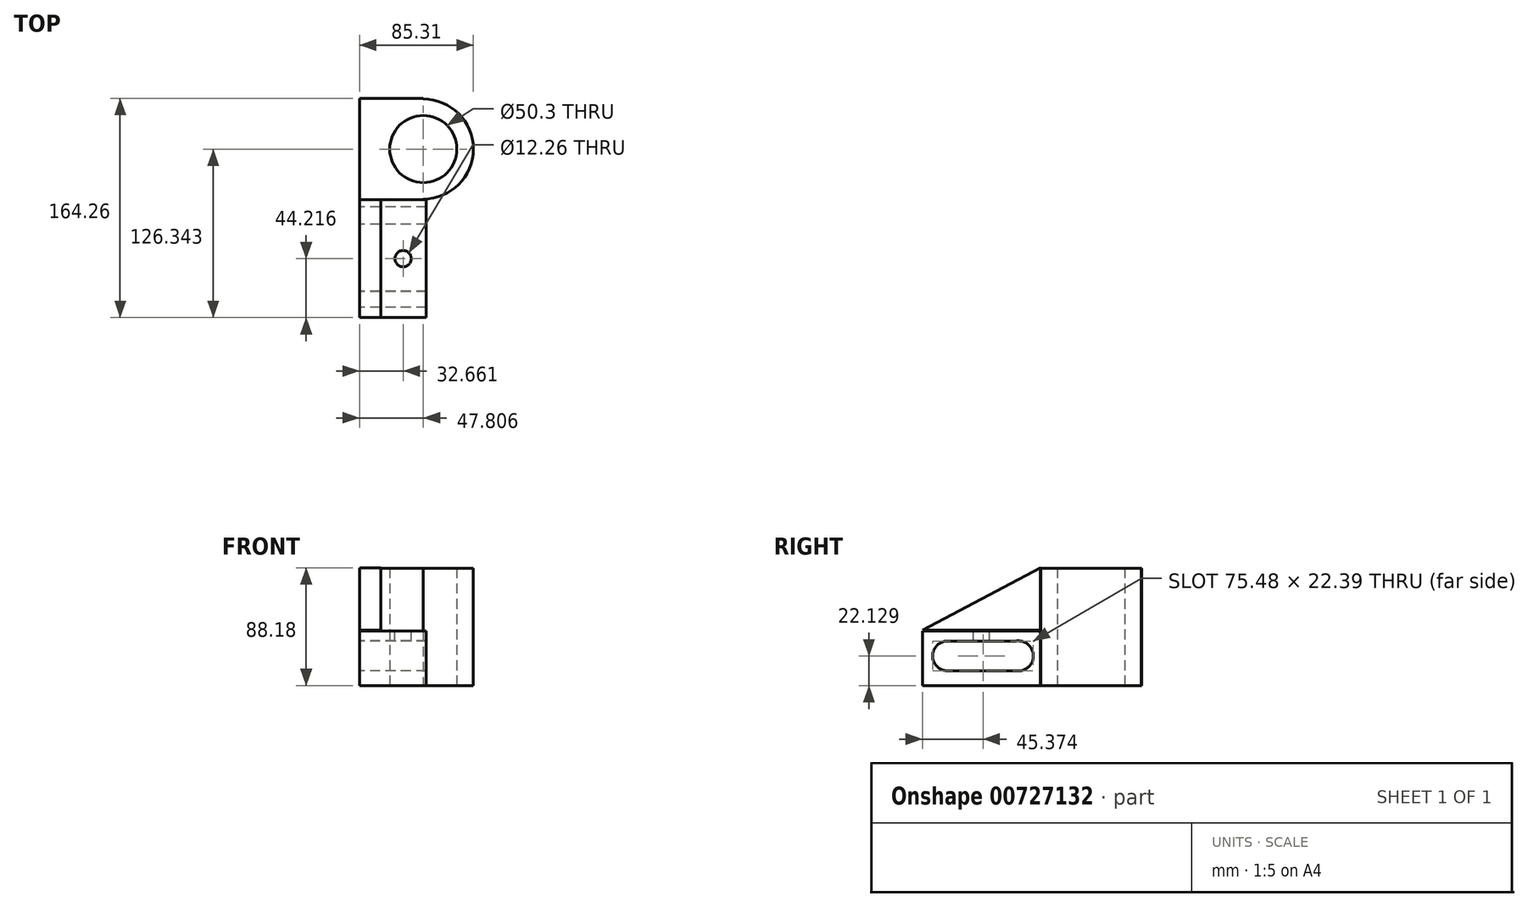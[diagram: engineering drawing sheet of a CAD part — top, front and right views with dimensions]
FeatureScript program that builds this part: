
annotation { "Feature Type Name" : "Feature", "Feature Type Description" : "" }
export const myFeature = defineFeature(function(context is Context, id is Id, definition is map)
    precondition{}
    {
        {
            var Q0;
            Q0=qCreatedBy(makeId("Top.planeOp"),FACE);
            var sketch = newSketch(context, id + "F0", { "sketchPlane" : qUnion([Q0])});
            skLineSegment(sketch, "E0.bottom", {"start": v(0, 0) * mm, "end": v(47.8, 0) * mm});
            skLineSegment(sketch, "E0.top", {"start": v(0, 75.83) * mm, "end": v(47.8, 75.83) * mm});
            skLineSegment(sketch, "E0.left", {"start": v(0, 0) * mm, "end": v(0, 75.83) * mm});
            skLineSegment(sketch, "E0.right", {"start": v(47.8, 0) * mm, "end": v(47.8, 0.4) * mm});
            skCircle(sketch, "E1", {"center": v(47.8, 37.91) * mm, "radius": 25.15 * mm});
            skArc(sketch, "E2", {"start": v(47.8, 0.4) * mm, "mid": v(85.31, 37.91) * mm, "end": v(47.8, 75.42) * mm});
            skLineSegment(sketch, "E3.trimOffspring", {"start": v(47.8, 75.42) * mm, "end": v(47.8, 75.83) * mm});
            skSolve(sketch);
        }
        {
            var Q0;
            Q0 = qSketchRegion(id + "F0", true);
            extrude(context, id + "F1", {"entities" : qUnion([Q0]), "depth" : 88 * mm, "offsetDistance" : 25 * mm});
        }
        {
            var Q0;
            Q0=qCreatedBy(makeId("Right.planeOp"),FACE);
            var sketch = newSketch(context, id + "F2", { "sketchPlane" : qUnion([Q0])});
            skLineSegment(sketch, "E4.bottom", {"start": v(0, 0) * mm, "end": v(-88.43, 0) * mm});
            skLineSegment(sketch, "E4.top", {"start": v(0, 40.75) * mm, "end": v(-88.43, 40.75) * mm});
            skLineSegment(sketch, "E4.left", {"start": v(0, 0) * mm, "end": v(0, 40.75) * mm});
            skLineSegment(sketch, "E4.right", {"start": v(-88.43, 0) * mm, "end": v(-88.43, 40.75) * mm});
            skArc(sketch, "E5", {"start": v(-16.59, 10.93) * mm, "mid": v(-5.32, 23.1) * mm, "end": v(-18.37, 33.33) * mm});
            skArc(sketch, "E6", {"start": v(-68.8, 33.33) * mm, "mid": v(-80.8, 22.11) * mm, "end": v(-68.62, 11.1) * mm});
            skLineSegment(sketch, "E7", {"start": v(-68.8, 33.33) * mm, "end": v(-18.37, 33.33) * mm});
            skLineSegment(sketch, "E8", {"start": v(-68.62, 11.1) * mm, "end": v(-16.59, 10.93) * mm});
            skSolve(sketch);
        }
        {
            var Q0;
            Q0=makeQuery(id+"F2.imprint","IMPRINT",FACE,{"disambiguationData":[TD([[makeQuery(id+"F2.imprint","IMPRINT",EDGE,{"derivedFrom":sQuery(id+"F2.wireOp",EDGE,"E4.bottom")}),-1.0]])]});
            extrude(context, id + "F3", {"entities" : qUnion([Q0]), "operationType" : NewBodyOperationType.ADD, "depth" : 50 * mm, "offsetDistance" : 25 * mm});
        }
        {
            var Q0;
            Q0=qCreatedBy(makeId("Right.planeOp"),FACE);
            var sketch = newSketch(context, id + "F4", { "sketchPlane" : qUnion([Q0])});
            skLineSegment(sketch, "E9", {"start": v(0, 41.38) * mm, "end": v(-88.19, 41.38) * mm});
            skLineSegment(sketch, "E10", {"start": v(-88.19, 41.38) * mm, "end": v(0, 88.18) * mm});
            skLineSegment(sketch, "E11", {"start": v(0, 88.18) * mm, "end": v(0, 41.38) * mm});
            skSolve(sketch);
        }
        {
            var Q0;
            Q0 = qSketchRegion(id + "F4", true);
            extrude(context, id + "F5", {"entities" : qUnion([Q0]), "operationType" : NewBodyOperationType.ADD, "depth" : 16 * mm, "offsetDistance" : 25 * mm});
        }
        {
            var Q0;
            Q0=makeQuery(id+"F3.opExtrude","SWEPT_FACE",FACE,{"disambiguationData":[OSD([sQuery(id+"F2.wireOp",EDGE,"E4.top")])]});
            var sketch = newSketch(context, id + "F6", { "sketchPlane" : qUnion([Q0])});
            skCircle(sketch, "E12", {"center": v(32.66, -44.21) * mm, "radius": 6.13 * mm});
            skPoint(sketch, "E12.centerSnap0", {"position": v(0, -44.21) * mm});
            skSolve(sketch);
        }
        {
            var Q0;
            Q0 = qSketchRegion(id + "F6", true);
            extrude(context, id + "F7", {"entities" : qUnion([Q0]), "operationType" : NewBodyOperationType.REMOVE, "endBound" : BoundingType.UP_TO_NEXT, "oppositeDirection" : true, "depth" : 25 * mm, "offsetDistance" : 25 * mm});
        }
    });
